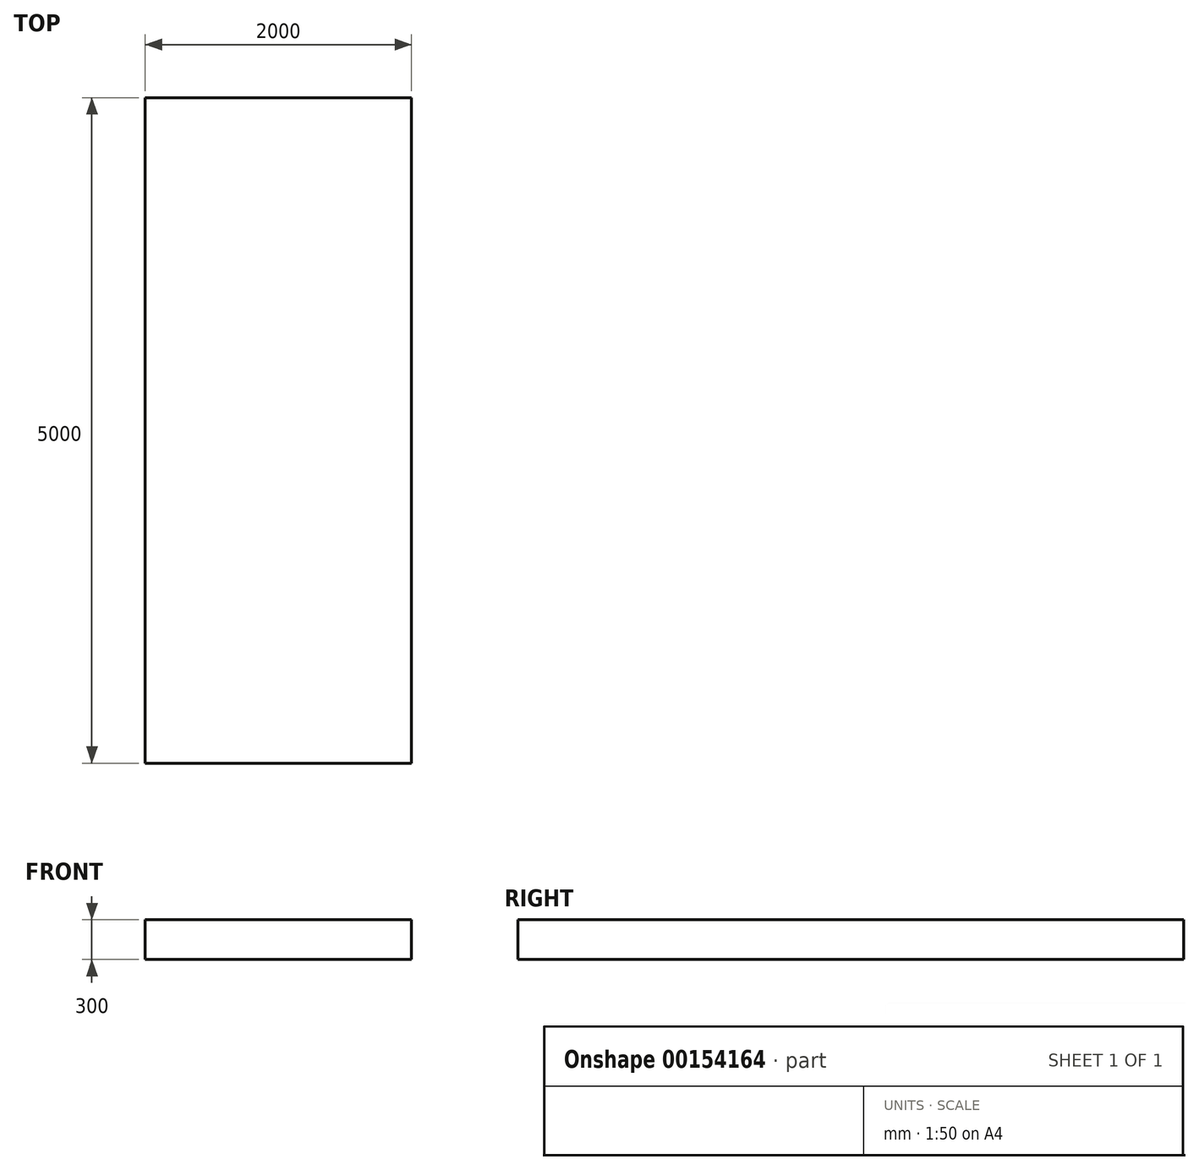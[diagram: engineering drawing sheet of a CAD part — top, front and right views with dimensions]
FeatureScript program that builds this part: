
annotation { "Feature Type Name" : "Feature", "Feature Type Description" : "" }
export const myFeature = defineFeature(function(context is Context, id is Id, definition is map)
    precondition{}
    {
        {
            var Q0;
            Q0=qCreatedBy(makeId("Front.planeOp"),FACE);
            var sketch = newSketch(context, id + "F0", { "sketchPlane" : qUnion([Q0])});
            skLineSegment(sketch, "E0.bottom", {"start": v(1000, -150) * mm, "end": v(-1000, -150) * mm});
            skLineSegment(sketch, "E0.top", {"start": v(1000, 150) * mm, "end": v(-1000, 150) * mm});
            skLineSegment(sketch, "E0.left", {"start": v(1000, -150) * mm, "end": v(1000, 150) * mm});
            skLineSegment(sketch, "E0.right", {"start": v(-1000, -150) * mm, "end": v(-1000, 150) * mm});
            skPoint(sketch, "E0.middle", {"position": v(0, 0) * mm});
            skSolve(sketch);
        }
        {
            var Q0;
            Q0=makeQuery(id+"F0.imprint","IMPRINT",FACE,{"disambiguationData":[TD([[makeQuery(id+"F0.imprint","IMPRINT",EDGE,{"derivedFrom":sQuery(id+"F0.wireOp",EDGE,"E0.bottom")}),-1.0]])]});
            extrude(context, id + "F1", {"entities" : qUnion([Q0]), "depth" : 5000 * mm});
        }
    });
